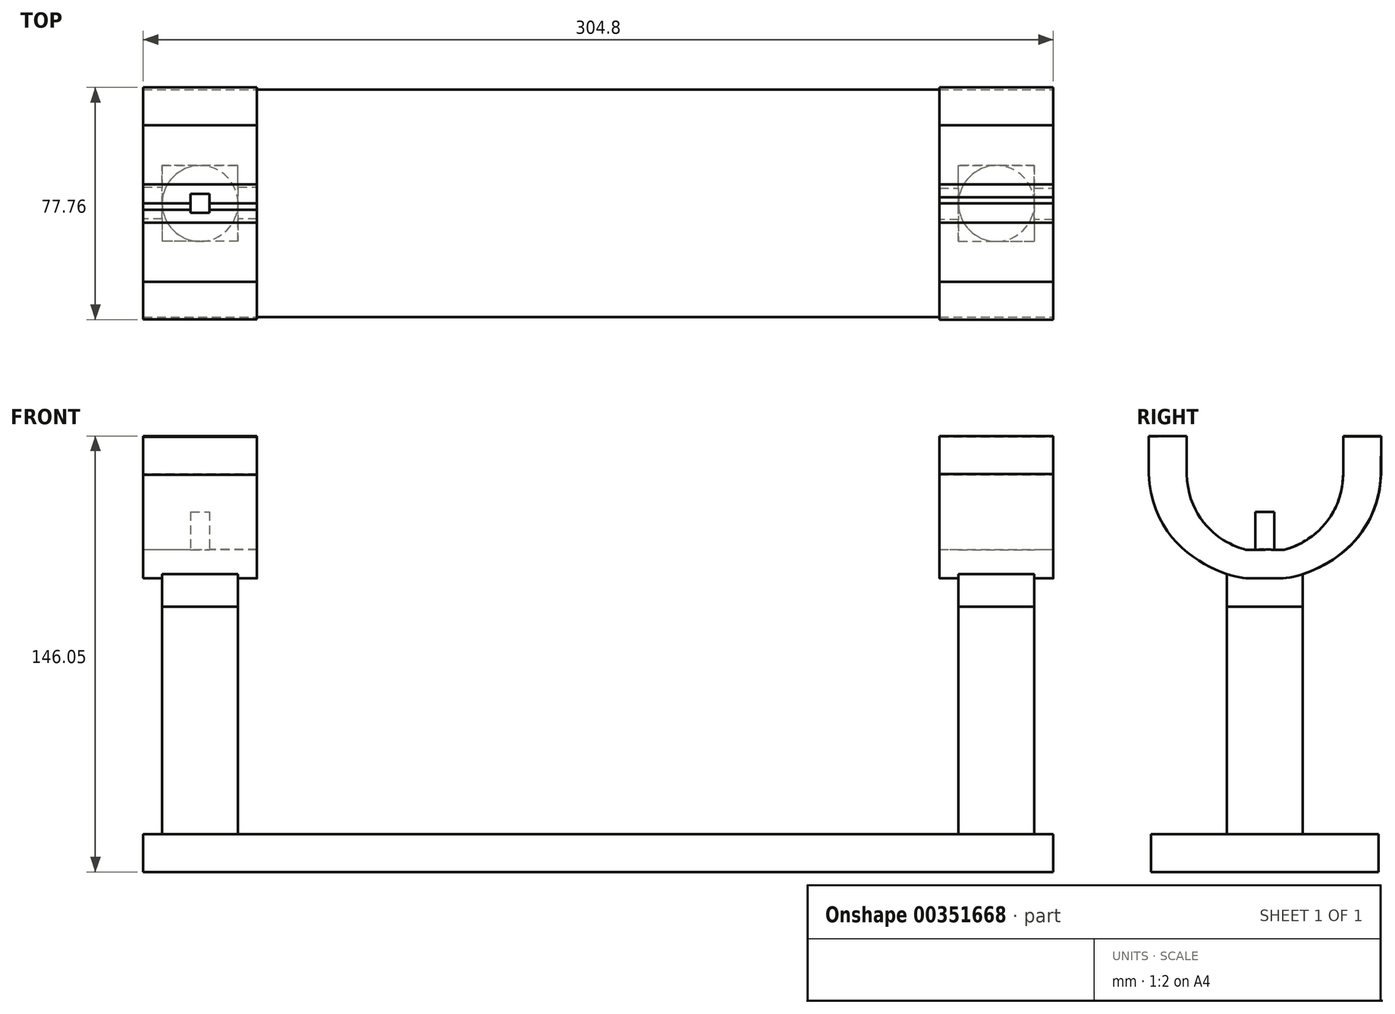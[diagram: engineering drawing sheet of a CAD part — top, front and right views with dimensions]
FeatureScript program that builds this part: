
annotation { "Feature Type Name" : "Feature", "Feature Type Description" : "" }
export const myFeature = defineFeature(function(context is Context, id is Id, definition is map)
    precondition{}
    {
        {
            var Q0;
            Q0=qCreatedBy(makeId("Front.planeOp"),FACE);
            var sketch = newSketch(context, id + "F0", { "sketchPlane" : qUnion([Q0])});
            skLineSegment(sketch, "E0.bottom", {"start": v(0, 0) * mm, "end": v(304.8, 0) * mm});
            skLineSegment(sketch, "E0.top", {"start": v(0, 12.7) * mm, "end": v(304.8, 12.7) * mm});
            skLineSegment(sketch, "E0.left", {"start": v(0, 0) * mm, "end": v(0, 12.7) * mm});
            skLineSegment(sketch, "E0.right", {"start": v(304.8, 0) * mm, "end": v(304.8, 12.7) * mm});
            skSolve(sketch);
        }
        {
            var Q0;
            Q0 = qSketchRegion(id + "F0", true);
            extrude(context, id + "F1", {"entities" : qUnion([Q0]), "oppositeDirection" : true, "depth" : 76.2 * mm});
        }
        {
            var Q0;
            Q0=makeQuery(id+"F1.opExtrude","SWEPT_FACE",FACE,{"disambiguationData":[OSD([sQuery(id+"F0.wireOp",EDGE,"E0.top")])]});
            var sketch = newSketch(context, id + "F2", { "sketchPlane" : qUnion([Q0])});
            skCircle(sketch, "E1", {"center": v(19.05, 38.1) * mm, "radius": 12.7 * mm});
            skCircle(sketch, "E2", {"center": v(285.75, 38.1) * mm, "radius": 12.7 * mm});
            skSolve(sketch);
        }
        {
            var Q0;
            Q0 = qSketchRegion(id + "F2", true);
            extrude(context, id + "F3", {"entities" : qUnion([Q0]), "operationType" : NewBodyOperationType.ADD, "depth" : 76.2 * mm});
        }
        {
            var Q0;
            Q0=makeQuery(id+"F3.opExtrude","CAP_FACE",FACE,{"disambiguationData":[OSD([sQuery(id+"F2.wireOp",EDGE,"E1")])],"isStart":false});
            var sketch = newSketch(context, id + "F4", { "sketchPlane" : qUnion([Q0])});
            skPoint(sketch, "E3", {"position": v(19.05, 38.1) * mm});
            skPoint(sketch, "E4", {"position": v(31.75, 50.8) * mm});
            skPoint(sketch, "E5", {"position": v(31.75, 25.4) * mm});
            skPoint(sketch, "E6", {"position": v(6.35, 25.4) * mm});
            skPoint(sketch, "E7", {"position": v(6.35, 50.8) * mm});
            skLineSegment(sketch, "E8", {"start": v(6.35, 50.8) * mm, "end": v(31.75, 50.8) * mm});
            skLineSegment(sketch, "E9", {"start": v(31.75, 25.4) * mm, "end": v(31.75, 50.8) * mm});
            skLineSegment(sketch, "E10", {"start": v(31.75, 25.4) * mm, "end": v(6.35, 25.4) * mm});
            skLineSegment(sketch, "E11", {"start": v(6.35, 50.8) * mm, "end": v(6.35, 25.4) * mm});
            skPoint(sketch, "E12.positionSnap0", {"position": v(31.75, 38.1) * mm});
            skLineSegment(sketch, "E13.MirrorCS", {"start": v(273.05, 25.4) * mm, "end": v(273.05, 50.8) * mm});
            skLineSegment(sketch, "E14.MirrorCS", {"start": v(273.05, 25.4) * mm, "end": v(298.45, 25.4) * mm});
            skLineSegment(sketch, "E15.MirrorCS", {"start": v(298.45, 50.8) * mm, "end": v(298.45, 25.4) * mm});
            skLineSegment(sketch, "E16.MirrorCS", {"start": v(298.45, 50.8) * mm, "end": v(273.05, 50.8) * mm});
            skSolve(sketch);
        }
        {
            var Q0;
            Q0 = qSketchRegion(id + "F4", true);
            extrude(context, id + "F5", {"entities" : qUnion([Q0]), "operationType" : NewBodyOperationType.ADD, "depth" : 19.05 * mm});
        }
        {
            var Q0;
            Q0=makeQuery(id+"F5.opExtrude","SWEPT_FACE",FACE,{"disambiguationData":[OSD([sQuery(id+"F4.wireOp",EDGE,"E11")])]});
            var sketch = newSketch(context, id + "F6", { "sketchPlane" : qUnion([Q0])});
            skPoint(sketch, "E17", {"position": v(-38.1, 133.35) * mm});
            skPoint(sketch, "E17.positionSnap0", {"position": v(-38.1, 107.95) * mm});
            skFitSpline(sketch, "E18", {"points": [v(-38.1, 107.95) * mm, v(-44.5, 107.95) * mm, v(-64.3, 133.35) * mm], "startDerivative": vector(-36.9, 0) * mm, "endDerivative": vector(-2.4, 78.23) * mm});
            skLineSegment(sketch, "E19", {"start": v(-64.3, 133.35) * mm, "end": v(-64.3, 146.05) * mm});
            skLineSegment(sketch, "E20", {"start": v(-44.5, 107.95) * mm, "end": v(-38.1, 107.95) * mm});
            skLineSegment(sketch, "E21.MirrorCS", {"start": v(-31.7, 107.95) * mm, "end": v(-38.1, 107.95) * mm});
            skLineSegment(sketch, "E22.MirrorCS", {"start": v(-11.9, 133.35) * mm, "end": v(-11.9, 146.05) * mm});
            skFitSpline(sketch, "E23.MirrorCS", {"points": [v(-38.1, 107.95) * mm, v(-31.7, 107.95) * mm, v(-11.9, 133.35) * mm], "startDerivative": vector(21.34, 2.75) * mm, "endDerivative": vector(0.95, 71.33) * mm});
            skPoint(sketch, "E24", {"position": v(-77, 146.05) * mm});
            skLineSegment(sketch, "E25", {"start": v(-77, 146.05) * mm, "end": v(-64.3, 146.05) * mm});
            skLineSegment(sketch, "E26", {"start": v(-77, 146.05) * mm, "end": v(-77, 133.35) * mm});
            skPoint(sketch, "E27", {"position": v(-44.5, 98.43) * mm});
            skFitSpline(sketch, "E28", {"points": [v(-38.32, 100.08) * mm, v(-44.5, 98.43) * mm, v(-77, 133.35) * mm], "startDerivative": vector(-35.64, -9.55) * mm, "endDerivative": vector(-3.44, 106.77) * mm});
            skLineSegment(sketch, "E29.MirrorCS", {"start": v(0.76, 145.76) * mm, "end": v(-11.94, 145.85) * mm});
            skLineSegment(sketch, "E30.MirrorCS", {"start": v(0.76, 145.76) * mm, "end": v(0.66, 133.06) * mm});
            skFitSpline(sketch, "E31.MirrorCS", {"points": [v(-38.26, 100.08) * mm, v(-32.1, 98.38) * mm, v(0.66, 133.06) * mm], "startDerivative": vector(35.56, -9.81) * mm, "endDerivative": vector(4.24, 106.74) * mm});
            skLineSegment(sketch, "E32", {"start": v(-44.5, 98.43) * mm, "end": v(-32.1, 98.38) * mm});
            skSolve(sketch);
        }
        {
            var Q0;
            Q0 = qSketchRegion(id + "F6", true);
            extrude(context, id + "F7", {"entities" : qUnion([Q0]), "operationType" : NewBodyOperationType.ADD, "oppositeDirection" : true, "depth" : 31.75 * mm, "hasSecondDirection" : true, "secondDirectionOppositeDirection" : false, "secondDirectionDepth" : 6.35 * mm});
        }
        {
            var Q0;
            Q0=makeQuery(id+"F7.boolean.opBoolean","MERGE",FACE,{"derivedFrom":[makeQuery(id+"F5.opExtrude","CAP_FACE",FACE,{"disambiguationData":[OSD([sQuery(id+"F4.wireOp",EDGE,"E8"),sQuery(id+"F4.wireOp",EDGE,"E9"),sQuery(id+"F4.wireOp",EDGE,"E10"),sQuery(id+"F4.wireOp",EDGE,"E11")])],"isStart":false}),makeQuery(id+"F7.opExtrude","SWEPT_FACE",FACE,{"disambiguationData":[OSD([sQuery(id+"F6.wireOp",EDGE,"E20"),sQuery(id+"F6.wireOp",EDGE,"E21.MirrorCS")])]})]});
            var sketch = newSketch(context, id + "F8", { "sketchPlane" : qUnion([Q0])});
            skLineSegment(sketch, "E33.bottom", {"start": v(15.88, 34.92) * mm, "end": v(22.23, 34.92) * mm});
            skLineSegment(sketch, "E33.top", {"start": v(15.88, 41.27) * mm, "end": v(22.23, 41.27) * mm});
            skLineSegment(sketch, "E33.left", {"start": v(15.88, 34.92) * mm, "end": v(15.88, 41.27) * mm});
            skLineSegment(sketch, "E33.right", {"start": v(22.23, 34.92) * mm, "end": v(22.23, 41.27) * mm});
            skSolve(sketch);
        }
        {
            var Q0;
            Q0 = qSketchRegion(id + "F8", true);
            extrude(context, id + "F9", {"entities" : qUnion([Q0]), "operationType" : NewBodyOperationType.ADD, "depth" : 12.7 * mm});
        }
        {
            var Q0;
            Q0=makeQuery(id+"F5.opExtrude","SWEPT_FACE",FACE,{"disambiguationData":[OSD([sQuery(id+"F4.wireOp",EDGE,"E15.MirrorCS")])]});
            var sketch = newSketch(context, id + "F10", { "sketchPlane" : qUnion([Q0])});
            skPoint(sketch, "E34", {"position": v(38.12, 133.35) * mm});
            skPoint(sketch, "E34.positionSnap0", {"position": v(38.12, 107.95) * mm});
            skFitSpline(sketch, "E35", {"points": [v(38.12, 107.95) * mm, v(31.72, 107.95) * mm, v(11.93, 133.35) * mm], "startDerivative": vector(-36.9, 0) * mm, "endDerivative": vector(-2.4, 78.23) * mm});
            skLineSegment(sketch, "E36", {"start": v(11.93, 133.35) * mm, "end": v(11.93, 146.05) * mm});
            skLineSegment(sketch, "E37", {"start": v(31.72, 107.95) * mm, "end": v(38.12, 107.95) * mm});
            skLineSegment(sketch, "E38.MirrorCS", {"start": v(44.52, 107.95) * mm, "end": v(38.12, 107.95) * mm});
            skLineSegment(sketch, "E39.MirrorCS", {"start": v(64.32, 133.35) * mm, "end": v(64.32, 146.05) * mm});
            skFitSpline(sketch, "E40.MirrorCS", {"points": [v(38.12, 107.95) * mm, v(44.52, 107.95) * mm, v(64.32, 133.35) * mm], "startDerivative": vector(21.34, 2.75) * mm, "endDerivative": vector(0.95, 71.33) * mm});
            skPoint(sketch, "E41", {"position": v(-0.77, 146.05) * mm});
            skLineSegment(sketch, "E42", {"start": v(-0.77, 146.05) * mm, "end": v(11.93, 146.05) * mm});
            skLineSegment(sketch, "E43", {"start": v(-0.77, 146.05) * mm, "end": v(-0.77, 133.35) * mm});
            skPoint(sketch, "E44", {"position": v(31.72, 98.42) * mm});
            skFitSpline(sketch, "E45", {"points": [v(37.9, 100.08) * mm, v(31.72, 98.42) * mm, v(-0.77, 133.35) * mm], "startDerivative": vector(-35.64, -9.55) * mm, "endDerivative": vector(-3.44, 106.77) * mm});
            skLineSegment(sketch, "E46.MirrorCS", {"start": v(76.98, 145.76) * mm, "end": v(64.28, 145.85) * mm});
            skLineSegment(sketch, "E47.MirrorCS", {"start": v(76.98, 145.76) * mm, "end": v(76.89, 133.06) * mm});
            skFitSpline(sketch, "E48.MirrorCS", {"points": [v(37.96, 100.08) * mm, v(44.13, 98.38) * mm, v(76.89, 133.06) * mm], "startDerivative": vector(35.56, -9.81) * mm, "endDerivative": vector(4.24, 106.74) * mm});
            skLineSegment(sketch, "E49", {"start": v(31.72, 98.42) * mm, "end": v(44.13, 98.38) * mm});
            skSolve(sketch);
        }
        {
            var Q0;
            Q0 = qSketchRegion(id + "F10", true);
            extrude(context, id + "F11", {"entities" : qUnion([Q0]), "operationType" : NewBodyOperationType.ADD, "oppositeDirection" : true, "depth" : 31.75 * mm, "hasSecondDirection" : true, "secondDirectionOppositeDirection" : false, "secondDirectionDepth" : 6.35 * mm});
        }
    });
